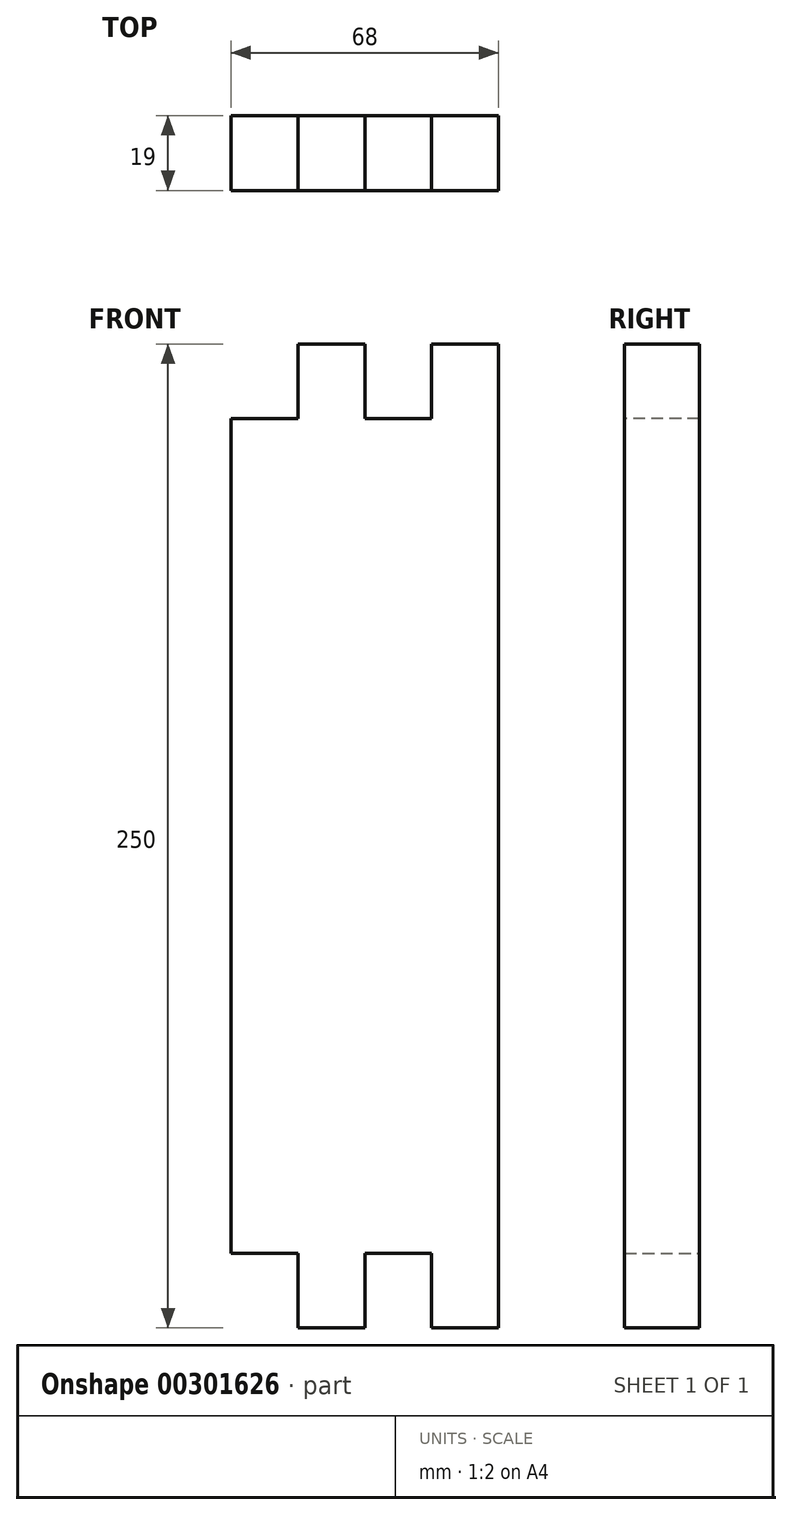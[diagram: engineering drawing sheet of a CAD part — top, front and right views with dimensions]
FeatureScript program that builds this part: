
annotation { "Feature Type Name" : "Feature", "Feature Type Description" : "" }
export const myFeature = defineFeature(function(context is Context, id is Id, definition is map)
    precondition{}
    {
        {
            var Q0;
            Q0=qCreatedBy(makeId("Front.planeOp"),FACE);
            var sketch = newSketch(context, id + "F0", { "sketchPlane" : qUnion([Q0])});
            skLineSegment(sketch, "E0.bottom", {"start": v(34, -125) * mm, "end": v(-34, -125) * mm});
            skLineSegment(sketch, "E0.top", {"start": v(34, 125) * mm, "end": v(-34, 125) * mm});
            skLineSegment(sketch, "E0.left", {"start": v(34, -125) * mm, "end": v(34, 125) * mm});
            skLineSegment(sketch, "E0.right", {"start": v(-34, -125) * mm, "end": v(-34, 125) * mm});
            skPoint(sketch, "E0.middle", {"position": v(0, 0) * mm});
            skSolve(sketch);
        }
        {
            var Q0;
            Q0 = qSketchRegion(id + "F0", true);
            extrude(context, id + "F1", {"entities" : qUnion([Q0]), "depth" : 19 * mm});
        }
        {
            var Q0;
            Q0=makeQuery(id+"F1.opExtrude","CAP_FACE",FACE,{"disambiguationData":[OSD([sQuery(id+"F0.wireOp",EDGE,"E0.bottom"),sQuery(id+"F0.wireOp",EDGE,"E0.top"),sQuery(id+"F0.wireOp",EDGE,"E0.left"),sQuery(id+"F0.wireOp",EDGE,"E0.right")])],"isStart":false});
            var sketch = newSketch(context, id + "F2", { "sketchPlane" : qUnion([Q0])});
            skLineSegment(sketch, "E1.bottom", {"start": v(-34, 125) * mm, "end": v(-17, 125) * mm});
            skLineSegment(sketch, "E1.top", {"start": v(-34, 106) * mm, "end": v(-17, 106) * mm});
            skLineSegment(sketch, "E1.left", {"start": v(-34, 125) * mm, "end": v(-34, 106) * mm});
            skLineSegment(sketch, "E1.right", {"start": v(-17, 125) * mm, "end": v(-17, 106) * mm});
            skLineSegment(sketch, "E2.bottom", {"start": v(-17, 125) * mm, "end": v(0, 125) * mm});
            skLineSegment(sketch, "E2.top", {"start": v(-17, 106) * mm, "end": v(0, 106) * mm});
            skLineSegment(sketch, "E2.right", {"start": v(0, 125) * mm, "end": v(0, 106) * mm});
            skPoint(sketch, "E3.oppositeSnap0", {"position": v(0, 125) * mm});
            skLineSegment(sketch, "E3.bottom", {"start": v(0, 125) * mm, "end": v(0, 125) * mm});
            skLineSegment(sketch, "E3.top", {"start": v(0, 106) * mm, "end": v(0, 106) * mm});
            skLineSegment(sketch, "E4.bottom", {"start": v(0, 125) * mm, "end": v(17, 125) * mm});
            skLineSegment(sketch, "E4.top", {"start": v(0, 106) * mm, "end": v(17, 106) * mm});
            skLineSegment(sketch, "E4.right", {"start": v(17, 125) * mm, "end": v(17, 106) * mm});
            skLineSegment(sketch, "E5.bottom", {"start": v(17, 125) * mm, "end": v(34, 125) * mm});
            skLineSegment(sketch, "E5.top", {"start": v(17, 106) * mm, "end": v(34, 106) * mm});
            skLineSegment(sketch, "E5.right", {"start": v(34, 125) * mm, "end": v(34, 106) * mm});
            skSolve(sketch);
        }
        {
            var Q0;
            Q0=makeQuery(id+"F2.imprint","IMPRINT",FACE,{"disambiguationData":[TD([[makeQuery(id+"F2.imprint","IMPRINT",EDGE,{"derivedFrom":sQuery(id+"F2.wireOp",EDGE,"E4.bottom")}),1.0]])]});
            var Q1;
            Q1=makeQuery(id+"F2.imprint","IMPRINT",FACE,{"disambiguationData":[TD([[makeQuery(id+"F2.imprint","IMPRINT",EDGE,{"derivedFrom":sQuery(id+"F2.wireOp",EDGE,"E1.bottom")}),1.0]])]});
            extrude(context, id + "F3", {"entities" : qUnion([Q0, Q1]), "operationType" : NewBodyOperationType.REMOVE, "endBound" : BoundingType.THROUGH_ALL, "oppositeDirection" : true, "depth" : 25 * mm});
        }
        {
            var Q0;
            Q0=makeQuery(id+"F1.opExtrude","CAP_FACE",FACE,{"disambiguationData":[OSD([sQuery(id+"F0.wireOp",EDGE,"E0.bottom"),sQuery(id+"F0.wireOp",EDGE,"E0.top"),sQuery(id+"F0.wireOp",EDGE,"E0.left"),sQuery(id+"F0.wireOp",EDGE,"E0.right")])],"isStart":true});
            var sketch = newSketch(context, id + "F4", { "sketchPlane" : qUnion([Q0])});
            skLineSegment(sketch, "E6.bottom", {"start": v(34, -125) * mm, "end": v(17, -125) * mm});
            skLineSegment(sketch, "E6.top", {"start": v(34, -106) * mm, "end": v(17, -106) * mm});
            skLineSegment(sketch, "E6.left", {"start": v(34, -125) * mm, "end": v(34, -106) * mm});
            skLineSegment(sketch, "E6.right", {"start": v(17, -125) * mm, "end": v(17, -106) * mm});
            skLineSegment(sketch, "E7.bottom", {"start": v(17, -125) * mm, "end": v(0, -125) * mm});
            skLineSegment(sketch, "E7.top", {"start": v(17, -106) * mm, "end": v(0, -106) * mm});
            skLineSegment(sketch, "E7.right", {"start": v(0, -125) * mm, "end": v(0, -106) * mm});
            skLineSegment(sketch, "E8.bottom", {"start": v(0, -125) * mm, "end": v(-17, -125) * mm});
            skLineSegment(sketch, "E8.top", {"start": v(0, -106) * mm, "end": v(-17, -106) * mm});
            skLineSegment(sketch, "E8.right", {"start": v(-17, -125) * mm, "end": v(-17, -106) * mm});
            skLineSegment(sketch, "E9.bottom", {"start": v(-17, -125) * mm, "end": v(-34, -125) * mm});
            skLineSegment(sketch, "E9.top", {"start": v(-17, -106) * mm, "end": v(-34, -106) * mm});
            skLineSegment(sketch, "E9.right", {"start": v(-34, -125) * mm, "end": v(-34, -106) * mm});
            skSolve(sketch);
        }
        {
            var Q0;
            Q0=makeQuery(id+"F4.imprint","IMPRINT",FACE,{"disambiguationData":[TD([[makeQuery(id+"F4.imprint","IMPRINT",EDGE,{"derivedFrom":sQuery(id+"F4.wireOp",EDGE,"E6.bottom")}),1.0]])]});
            var Q1;
            Q1=makeQuery(id+"F4.imprint","IMPRINT",FACE,{"disambiguationData":[TD([[makeQuery(id+"F4.imprint","IMPRINT",EDGE,{"derivedFrom":sQuery(id+"F4.wireOp",EDGE,"E8.bottom")}),1.0]])]});
            extrude(context, id + "F5", {"entities" : qUnion([Q0, Q1]), "operationType" : NewBodyOperationType.REMOVE, "endBound" : BoundingType.THROUGH_ALL, "oppositeDirection" : true, "depth" : 25 * mm});
        }
    });
